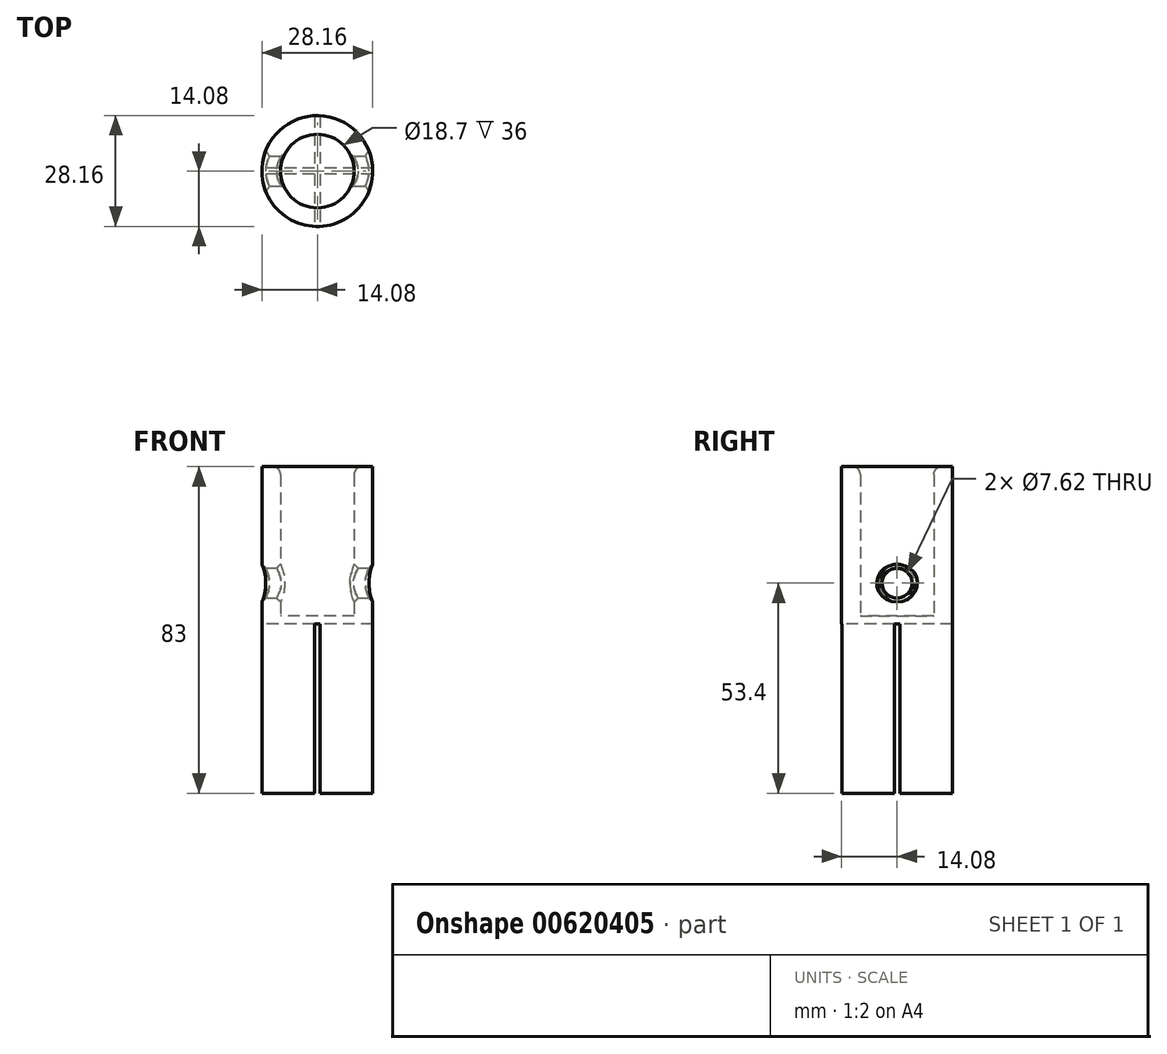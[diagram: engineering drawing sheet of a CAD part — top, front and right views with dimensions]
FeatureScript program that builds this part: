
annotation { "Feature Type Name" : "Feature", "Feature Type Description" : "" }
export const myFeature = defineFeature(function(context is Context, id is Id, definition is map)
    precondition{}
    {
        {
            var Q0;
            Q0=qCreatedBy(makeId("Top.planeOp"),FACE);
            var sketch = newSketch(context, id + "F0", { "sketchPlane" : qUnion([Q0])});
            skCircle(sketch, "E0", {"center": v(0, 0) * mm, "radius": 9.35 * mm});
            skCircle(sketch, "E1", {"center": v(0, 0) * mm, "radius": 14.08 * mm});
            skSolve(sketch);
        }
        {
            var Q0;
            Q0=makeQuery(id+"F0.imprint","IMPRINT",FACE,{"disambiguationData":[TD([[makeQuery(id+"F0.imprint","IMPRINT",EDGE,{"derivedFrom":sQuery(id+"F0.wireOp",EDGE,"E0")}),-1.0]])]});
            extrude(context, id + "F1", {"entities" : qUnion([Q0]), "depth" : 38 * mm, "offsetDistance" : 25 * mm});
        }
        {
            var Q0;
            Q0=makeQuery(id+"F0.imprint","IMPRINT",FACE,{"disambiguationData":[TD([[makeQuery(id+"F0.imprint","IMPRINT",EDGE,{"derivedFrom":sQuery(id+"F0.wireOp",EDGE,"E0")}),-1.0]])]});
            var Q1;
            Q1=makeQuery(id+"F0.imprint","IMPRINT",FACE,{"disambiguationData":[TD([[makeQuery(id+"F0.imprint","IMPRINT",EDGE,{"derivedFrom":sQuery(id+"F0.wireOp",EDGE,"E0")}),1.0]])]});
            extrude(context, id + "F2", {"entities" : qUnion([Q0, Q1]), "operationType" : NewBodyOperationType.ADD, "oppositeDirection" : true, "depth" : 45 * mm, "offsetDistance" : 25 * mm});
        }
        {
            var Q0;
            Q0=makeQuery(id+"F2.opExtrude","CAP_FACE",FACE,{"disambiguationData":[OSD([sQuery(id+"F0.wireOp",EDGE,"E1")])],"isStart":false});
            var sketch = newSketch(context, id + "F3", { "sketchPlane" : qUnion([Q0])});
            skLineSegment(sketch, "E2.bottom", {"start": v(0.7, -23.14) * mm, "end": v(-0.7, -23.14) * mm});
            skLineSegment(sketch, "E2.top", {"start": v(0.7, 23.14) * mm, "end": v(-0.7, 23.14) * mm});
            skLineSegment(sketch, "E2.left", {"start": v(0.7, -23.14) * mm, "end": v(0.7, -0.7) * mm});
            skLineSegment(sketch, "E2.right", {"start": v(-0.7, -23.14) * mm, "end": v(-0.7, -0.7) * mm});
            skPoint(sketch, "E2.middle", {"position": v(0, 0) * mm});
            skLineSegment(sketch, "E3.bottom", {"start": v(30.63, -0.7) * mm, "end": v(0.7, -0.7) * mm});
            skLineSegment(sketch, "E3.top", {"start": v(30.63, 0.7) * mm, "end": v(0.7, 0.7) * mm});
            skLineSegment(sketch, "E3.left", {"start": v(30.63, -0.7) * mm, "end": v(30.63, 0.7) * mm});
            skLineSegment(sketch, "E3.right", {"start": v(-30.63, -0.7) * mm, "end": v(-30.63, 0.7) * mm});
            skLineSegment(sketch, "E4.trimOffspring", {"start": v(-0.7, 0.7) * mm, "end": v(-30.63, 0.7) * mm});
            skLineSegment(sketch, "E5.trimOffspring", {"start": v(-0.7, 0.7) * mm, "end": v(-0.7, 23.14) * mm});
            skLineSegment(sketch, "E6.trimOffspring", {"start": v(-0.7, -0.7) * mm, "end": v(-30.63, -0.7) * mm});
            skLineSegment(sketch, "E7.trimOffspring", {"start": v(0.7, 0.7) * mm, "end": v(0.7, 23.14) * mm});
            skSolve(sketch);
        }
        {
            var Q0;
            {var subQ0=sQuery(id+"F3.wireOp",EDGE,"E2.left");var subQ9=sQuery(id+"F3.wireOp",EDGE,"E3.bottom");var subQ14=makeQuery(id+"F3.imprint","INTERSECT",VERTEX,{"derivedFrom":[subQ0,subQ9]});Q0=makeQuery(id+"F3.imprint","IMPRINT",FACE,{"disambiguationData":[TD([[makeQuery(id+"F3.imprint","IMPRINT",EDGE,{"disambiguationData":[TD([[subQ14,1.0]])],"derivedFrom":subQ0}),1.0]])]});}
            var Q1;
            {var subQ0=sQuery(id+"F3.wireOp",EDGE,"E3.right");Q1=makeQuery(id+"F3.imprint","IMPRINT",FACE,{"disambiguationData":[TD([[makeQuery(id+"F3.imprint","IMPRINT",EDGE,{"derivedFrom":subQ0}),-1.0]])]});}
            var Q2;
            {var subQ0=sQuery(id+"F3.wireOp",EDGE,"E2.top");Q2=makeQuery(id+"F3.imprint","IMPRINT",FACE,{"disambiguationData":[TD([[makeQuery(id+"F3.imprint","IMPRINT",EDGE,{"derivedFrom":subQ0}),1.0]])]});}
            var Q3;
            {var subQ0=sQuery(id+"F3.wireOp",EDGE,"E3.left");Q3=makeQuery(id+"F3.imprint","IMPRINT",FACE,{"disambiguationData":[TD([[makeQuery(id+"F3.imprint","IMPRINT",EDGE,{"derivedFrom":subQ0}),1.0]])]});}
            var Q4;
            {var subQ0=sQuery(id+"F3.wireOp",EDGE,"E2.bottom");Q4=makeQuery(id+"F3.imprint","IMPRINT",FACE,{"disambiguationData":[TD([[makeQuery(id+"F3.imprint","IMPRINT",EDGE,{"derivedFrom":subQ0}),-1.0]])]});}
            extrude(context, id + "F4", {"entities" : qUnion([Q0, Q1, Q2, Q3, Q4]), "operationType" : NewBodyOperationType.REMOVE, "oppositeDirection" : true, "depth" : 44.4 * mm, "offsetDistance" : 25 * mm});
        }
        {
            var Q0;
            Q0=qCreatedBy(makeId("Right.planeOp"),FACE);
            var sketch = newSketch(context, id + "F5", { "sketchPlane" : qUnion([Q0])});
            skLineSegment(sketch, "E8", {"start": v(0, 0) * mm, "end": v(0, 8.4) * mm, "construction": true});
            skCircle(sketch, "E9", {"center": v(0, 8.4) * mm, "radius": 3.81 * mm});
            skSolve(sketch);
        }
        {
            var Q0;
            Q0=makeQuery(id+"F5.imprint","IMPRINT",FACE,{"disambiguationData":[TD([[makeQuery(id+"F5.imprint","IMPRINT",EDGE,{"derivedFrom":sQuery(id+"F5.wireOp",EDGE,"E9")}),1.0]])]});
            extrude(context, id + "F6", {"entities" : qUnion([Q0]), "operationType" : NewBodyOperationType.REMOVE, "endBound" : BoundingType.SYMMETRIC, "oppositeDirection" : true, "depth" : 52.2 * mm, "offsetDistance" : 25 * mm});
        }
        {
            var Q0;
            Q0=makeQuery(id+"F1.opExtrude","CAP_EDGE",EDGE,{"disambiguationData":[OSD([sQuery(id+"F0.wireOp",EDGE,"E0")])],"isStart":false});
            fillet(context, id + "F7", {"entities" : qUnion([Q0]), "radius" : 2 * mm, "tangentPropagation" : true, "allowEdgeOverflow" : false});
        }
        {
            var Q0;
            Q0=makeQuery(id+"F4.boolean.opBoolean","COPY",FACE,{"derivedFrom":makeQuery(id+"F4.opExtrude","CAP_FACE",FACE,{"disambiguationData":[OSD([sQuery(id+"F3.wireOp",EDGE,"E2.bottom"),sQuery(id+"F3.wireOp",EDGE,"E2.top"),sQuery(id+"F3.wireOp",EDGE,"E2.left"),sQuery(id+"F3.wireOp",EDGE,"E2.right"),sQuery(id+"F3.wireOp",EDGE,"E3.bottom"),sQuery(id+"F3.wireOp",EDGE,"E3.top"),sQuery(id+"F3.wireOp",EDGE,"E3.left"),sQuery(id+"F3.wireOp",EDGE,"E3.right"),sQuery(id+"F3.wireOp",EDGE,"E4.trimOffspring"),sQuery(id+"F3.wireOp",EDGE,"E5.trimOffspring"),sQuery(id+"F3.wireOp",EDGE,"E6.trimOffspring"),sQuery(id+"F3.wireOp",EDGE,"E7.trimOffspring")])],"isStart":false})});
            extrude(context, id + "F8", {"entities" : qUnion([Q0]), "operationType" : NewBodyOperationType.ADD, "depth" : 1.36 * mm, "offsetDistance" : 25 * mm});
        }
        {
            var Q0;
            Q0=makeQuery(id+"F6.boolean.opBoolean","INTERSECT",EDGE,{"disambiguationData":[OD(0.0)],"derivedFrom":[makeQuery(id+"F1.opExtrude","SWEPT_FACE",FACE,{"disambiguationData":[OSD([sQuery(id+"F0.wireOp",EDGE,"E0")])]}),makeQuery(id+"F6.opExtrude","SWEPT_FACE",FACE,{"disambiguationData":[OSD([sQuery(id+"F5.wireOp",EDGE,"E9")])]})]});
            var Q1;
            {var subQ0=sQuery(id+"F0.wireOp",EDGE,"E1");Q1=makeQuery(id+"F6.boolean.opBoolean","INTERSECT",EDGE,{"disambiguationData":[OD(0.0)],"derivedFrom":[makeQuery(id+"F2.boolean.opBoolean","MERGE",FACE,{"derivedFrom":[makeQuery(id+"F1.opExtrude","SWEPT_FACE",FACE,{"disambiguationData":[OSD([subQ0])]}),makeQuery(id+"F2.opExtrude","SWEPT_FACE",FACE,{"disambiguationData":[OSD([subQ0])]})]}),makeQuery(id+"F6.opExtrude","SWEPT_FACE",FACE,{"disambiguationData":[OSD([sQuery(id+"F5.wireOp",EDGE,"E9")])]})]});}
            var Q2;
            {var subQ0=sQuery(id+"F0.wireOp",EDGE,"E1");Q2=makeQuery(id+"F6.boolean.opBoolean","INTERSECT",EDGE,{"disambiguationData":[OD(1.0)],"derivedFrom":[makeQuery(id+"F2.boolean.opBoolean","MERGE",FACE,{"derivedFrom":[makeQuery(id+"F1.opExtrude","SWEPT_FACE",FACE,{"disambiguationData":[OSD([subQ0])]}),makeQuery(id+"F2.opExtrude","SWEPT_FACE",FACE,{"disambiguationData":[OSD([subQ0])]})]}),makeQuery(id+"F6.opExtrude","SWEPT_FACE",FACE,{"disambiguationData":[OSD([sQuery(id+"F5.wireOp",EDGE,"E9")])]})]});}
            var Q3;
            Q3=makeQuery(id+"F6.boolean.opBoolean","INTERSECT",EDGE,{"disambiguationData":[OD(1.0)],"derivedFrom":[makeQuery(id+"F1.opExtrude","SWEPT_FACE",FACE,{"disambiguationData":[OSD([sQuery(id+"F0.wireOp",EDGE,"E0")])]}),makeQuery(id+"F6.opExtrude","SWEPT_FACE",FACE,{"disambiguationData":[OSD([sQuery(id+"F5.wireOp",EDGE,"E9")])]})]});
            chamfer(context, id + "F9", {"entities" : qUnion([Q0, Q1, Q2, Q3]), "width" : 1 * mm, "tangentPropagation" : true});
        }
    });
